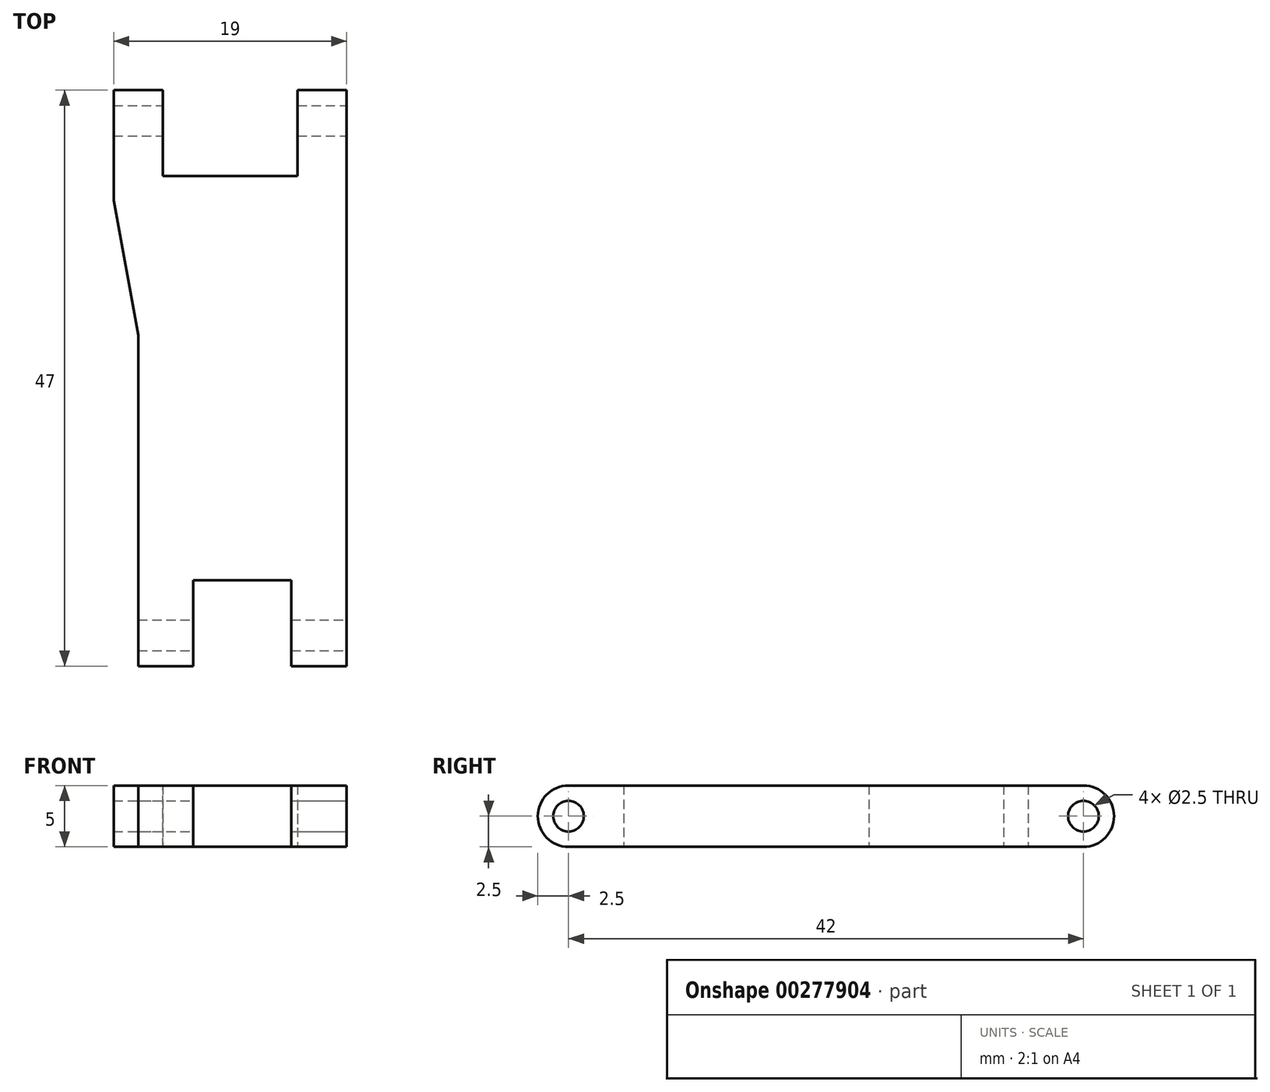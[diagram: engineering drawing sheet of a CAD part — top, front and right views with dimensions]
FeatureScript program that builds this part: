
annotation { "Feature Type Name" : "Feature", "Feature Type Description" : "" }
export const myFeature = defineFeature(function(context is Context, id is Id, definition is map)
    precondition{}
    {
        {
            var Q0;
            Q0=qCreatedBy(makeId("Top.planeOp"),FACE);
            var sketch = newSketch(context, id + "F0", { "sketchPlane" : qUnion([Q0])});
            skLineSegment(sketch, "E0", {"start": v(-8.5, 0) * mm, "end": v(-4, 0) * mm});
            skLineSegment(sketch, "E1", {"start": v(8.5, 0) * mm, "end": v(8.5, 47) * mm});
            skLineSegment(sketch, "E2", {"start": v(8.5, 47) * mm, "end": v(4.5, 47) * mm});
            skLineSegment(sketch, "E3", {"start": v(-4, 0) * mm, "end": v(-4, 7) * mm});
            skLineSegment(sketch, "E4", {"start": v(-4, 7) * mm, "end": v(4, 7) * mm});
            skLineSegment(sketch, "E5", {"start": v(4, 7) * mm, "end": v(4, 0) * mm});
            skLineSegment(sketch, "E6.trimOffspring", {"start": v(4, 0) * mm, "end": v(8.5, 0) * mm});
            skLineSegment(sketch, "E7", {"start": v(0, 0) * mm, "end": v(0, 7) * mm, "construction": true});
            skLineSegment(sketch, "E8", {"start": v(-8.5, 0) * mm, "end": v(-8.5, 27) * mm});
            skLineSegment(sketch, "E9", {"start": v(-10.5, 47) * mm, "end": v(-10.5, 38) * mm});
            skLineSegment(sketch, "E10", {"start": v(-10.5, 38) * mm, "end": v(-8.5, 27) * mm});
            skLineSegment(sketch, "E11", {"start": v(-6.5, 47) * mm, "end": v(-6.5, 40) * mm});
            skLineSegment(sketch, "E12", {"start": v(-6.5, 40) * mm, "end": v(4.5, 40) * mm});
            skLineSegment(sketch, "E13", {"start": v(4.5, 40) * mm, "end": v(4.5, 47) * mm});
            skLineSegment(sketch, "E14.trimOffspring", {"start": v(-6.5, 47) * mm, "end": v(-10.5, 47) * mm});
            skSolve(sketch);
        }
        {
            var Q0;
            Q0 = qSketchRegion(id + "F0", true);
            extrude(context, id + "F1", {"entities" : qUnion([Q0]), "depth" : 5 * mm, "symmetric" : true});
        }
        {
            var Q0;
            Q0=qCreatedBy(makeId("Right.planeOp"),FACE);
            var sketch = newSketch(context, id + "F2", { "sketchPlane" : qUnion([Q0])});
            skCircle(sketch, "E15", {"center": v(2.5, 0) * mm, "radius": 1.25 * mm});
            skArc(sketch, "E16", {"start": v(2.5, 2.5) * mm, "mid": v(0, 0) * mm, "end": v(2.5, -2.5) * mm});
            skCircle(sketch, "E17", {"center": v(44.5, 0) * mm, "radius": 1.25 * mm});
            skArc(sketch, "E18", {"start": v(44.5, -2.5) * mm, "mid": v(47, 0) * mm, "end": v(44.5, 2.5) * mm});
            skLineSegment(sketch, "E19", {"start": v(2.5, 2.5) * mm, "end": v(0, 2.5) * mm});
            skLineSegment(sketch, "E20", {"start": v(0, 2.5) * mm, "end": v(0, -2.5) * mm});
            skLineSegment(sketch, "E21", {"start": v(0, -2.5) * mm, "end": v(2.5, -2.5) * mm});
            skLineSegment(sketch, "E22", {"start": v(44.5, 2.5) * mm, "end": v(47, 2.5) * mm});
            skLineSegment(sketch, "E23", {"start": v(47, 2.5) * mm, "end": v(47, -2.5) * mm});
            skLineSegment(sketch, "E24", {"start": v(47, -2.5) * mm, "end": v(44.5, -2.5) * mm});
            skSolve(sketch);
        }
        {
            var Q0;
            Q0 = qSketchRegion(id + "F2", true);
            extrude(context, id + "F3", {"entities" : qUnion([Q0]), "operationType" : NewBodyOperationType.REMOVE, "endBound" : BoundingType.THROUGH_ALL, "oppositeDirection" : true, "depth" : 25 * mm, "hasSecondDirection" : true, "secondDirectionBound" : BoundingType.THROUGH_ALL, "secondDirectionOppositeDirection" : false, "secondDirectionDepth" : 25 * mm});
        }
    });
